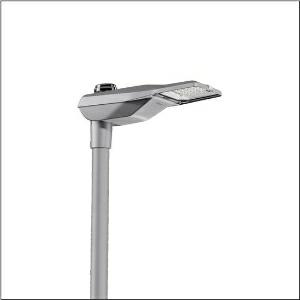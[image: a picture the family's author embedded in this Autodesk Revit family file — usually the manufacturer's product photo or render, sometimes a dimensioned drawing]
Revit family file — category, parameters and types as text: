
# Revit family: streetlight_sl_21_micro___st1_5a_5xe5p37n08cb_e60d
name_source: partatom
category: Lighting Fixtures
units: mm (PartAtom-declared; Revit-internal decimal feet)

## family parameters
Cut with Voids When Loaded = No
Host = Face
Light Source = No
Part Type = Normal
Room Calculation Point = No
Round Connector Dimension = Use Diameter
Shared = No

## types (1)
- --- (1 x LED, 2250 lm, 15.8 W, 3000K)
    Apparent Load = 16 VA
    CIE Flux Codes = 22 53 95 100 100
    Color Rendering = 70
    Color Temperature = 3000K
    Default Elevation = 1800 mm
    Description = Streetlight SL 21 micro, mast luminaire, primary light control with lens, of PMMA, primary optical cover: cover, of toughened safety glass, transparent, light distribution: ST1.5a, light emission: direct distribution, primary light characteristic: asymmetric, installation type: post-top, LED, 3G 1.5mm², High Power LED, rated luminous flux: 2.250lm, luminous efficacy: 142lm/W, light colour: 730, colour temperature: 3000K, control gear: NEMA (7pin), control: overheat protection, pre-setting: linear dimming characteristic, constant luminous flux control, time-dependent luminous flux control, flexible luminous flux parameterisation, mains connection: 230..240V, AC, 50/60Hz, connection cable pre-assembled, cable length: 6,5m, wiring characteristics: H07RN-F, start of lifetime: 16W, end of service life: 16W, reduction: 8W, luminaire housing, of diecast aluminium (EN AC-44300), powder-coated, SITECO metallic grey (DB 702S), corrosivity category C5 high according to DIN EN ISO 12944, multi-level sealing system, sealing non-destructively replaceable, inclination adjustable: 0°, 5°, 10°, 15°, length: 528mm, width: 235mm, height: 110mm, spigot size: 76/60mm (post-top), mounting height: 4..8m, protection rating (complete): IP66, insulation class (complete): insulation class I (protective earthing), certification: CE, ENEC, ENEC+, VDE, impact resistance: IK10, permissible operating ambient temperature for outdoor applications: -40..+50°C, standard-compliant lighting for roads and squares, packaging unit: 1 piece

Light Distribution: ST1.5a
    Height = 110 mm
    Lamp = 1 x LED
    Lamp Light Flux = 2250 lm
    Lamp Power = 15.8 W
    Lamp count = 1
    Length = 528 mm
    Luminous efficacy = 142 lm/W
    Manufacturer = Siteco
    ModVariant = No
    Model = 5XE5P37N08CB
    Number of Poles = 1
    OnlyDefault = Yes
    Power Factor = 1
    Product Name = Streetlight SL 21 micro | ST1.5a
    Product group = mast luminaire | pylon top
    ProductGroupID = 6100
    Protection Class = Protection class I
    Protection Degree = IP 66
    RLX_Detail_Level = 1
    RLX_Emergency_Light_Flux = 0 lm
    RLX_Emergency_Type = 0
    RLX_Emergency_Type_DB = No
    RlxData = <blob elided: 102557 chars, md5=7b8010c2>
    Socket = socket
    Standby Power = 0 W
    System Light Flux = 2250 lm
    System Power = 16 W
    Type Comments = factory setting: luminous flux: 100 % | dim-lin: 254 | 300 mA
    Type Image = l_1294375.jpg
    URL = http://relux.com
    VarID = @adj_133299
    Voltage = 0 V
    Weight = 0.00 kg
    Width = 235 mm

## geometry (parser evidence)
native form markers: Blend x4, Sweep x11
no freeform markers — native parametric forms only
